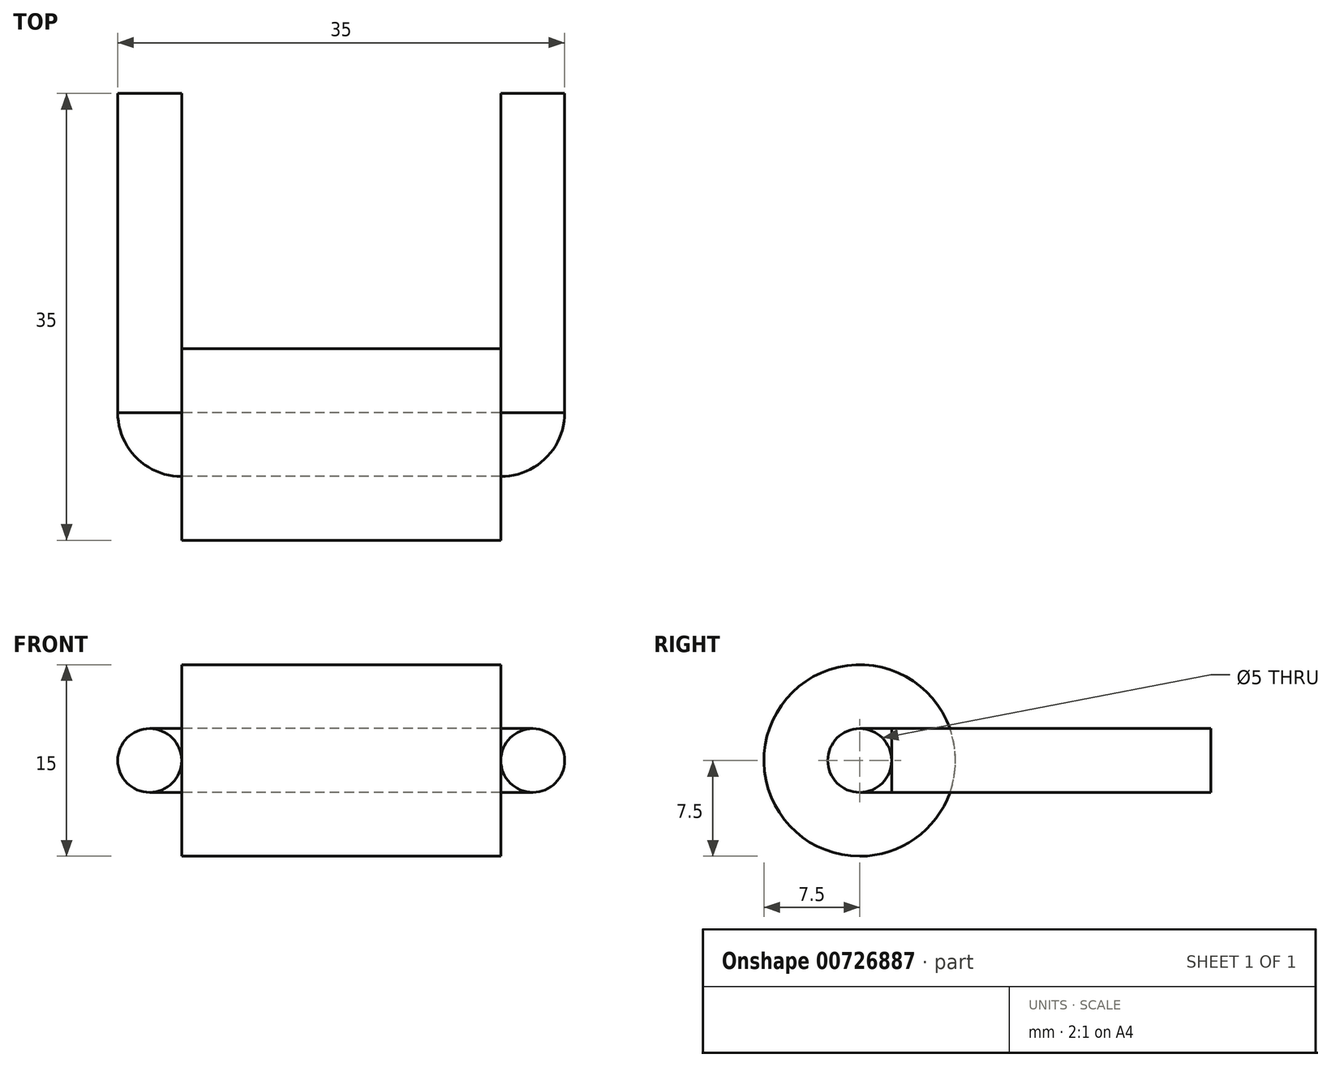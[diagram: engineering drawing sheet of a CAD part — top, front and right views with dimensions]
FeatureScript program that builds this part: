
annotation { "Feature Type Name" : "Feature", "Feature Type Description" : "" }
export const myFeature = defineFeature(function(context is Context, id is Id, definition is map)
    precondition{}
    {
        {
            var Q0;
            Q0=qCreatedBy(makeId("Front.planeOp"),FACE);
            var sketch = newSketch(context, id + "F0", { "sketchPlane" : qUnion([Q0])});
            skCircle(sketch, "E0", {"center": v(0, 0) * mm, "radius": 2.5 * mm});
            skLineSegment(sketch, "E1", {"start": v(0.18, 0) * mm, "end": v(2.5, 0) * mm});
            skCircle(sketch, "E2", {"center": v(30, 0) * mm, "radius": 2.5 * mm});
            skLineSegment(sketch, "E3.trimOffspring", {"start": v(27.5, 0) * mm, "end": v(30, 0) * mm});
            skSolve(sketch);
        }
        {
            var Q0;
            Q0 = qSketchRegion(id + "F0", true);
            extrude(context, id + "F1", {"entities" : qUnion([Q0]), "depth" : 25 * mm, "offsetDistance" : 25 * mm});
        }
        {
            var Q0;
            Q0=qCreatedBy(makeId("Front.planeOp"),FACE);
            cPlane(context, id + "F2", {"entities" : qUnion([Q0]), "cplaneType" : CPlaneType.OFFSET, "offset" : 27.5 * mm, "width" : 150 * mm, "height" : 150 * mm});
        }
        {
            var Q0;
            Q0=qCreatedBy(id+"F2.planeOp",FACE);
            var sketch = newSketch(context, id + "F3", { "sketchPlane" : qUnion([Q0])});
            skLineSegment(sketch, "E4", {"start": v(2.5, 0) * mm, "end": v(2.5, 2.5) * mm});
            skLineSegment(sketch, "E5", {"start": v(2.5, 2.5) * mm, "end": v(27.5, 2.5) * mm});
            skLineSegment(sketch, "E6", {"start": v(27.5, 2.5) * mm, "end": v(27.5, 0) * mm});
            skLineSegment(sketch, "E7", {"start": v(27.5, 0) * mm, "end": v(2.5, 0) * mm});
            skSolve(sketch);
        }
        {
            var Q0;
            Q0=makeQuery(id+"F3.imprint","IMPRINT",FACE,{"disambiguationData":[TD([[makeQuery(id+"F3.imprint","IMPRINT",EDGE,{"derivedFrom":sQuery(id+"F3.wireOp",EDGE,"E4")}),-1.0]])]});
            var Q1;
            Q1=sQuery(id+"F3.wireOp",EDGE,"E7");
            revolve(context, id + "F4", {"surfaceOperationType" : NewSurfaceOperationType.NEW, "entities" : qUnion([Q0]), "axis" : qUnion([Q1]), "revolveType" : RevolveType.FULL});
        }
        {
            var Q0;
            Q0=qCreatedBy(makeId("Top.planeOp"),FACE);
            var sketch = newSketch(context, id + "F5", { "sketchPlane" : qUnion([Q0])});
            skArc(sketch, "E8", {"start": v(0, -25) * mm, "mid": v(0.73, -26.77) * mm, "end": v(2.5, -27.5) * mm});
            skArc(sketch, "E9", {"start": v(27.5, -27.5) * mm, "mid": v(29.27, -26.77) * mm, "end": v(30, -25) * mm});
            skSolve(sketch);
        }
        {
            var Q0;
            Q0=makeQuery(id+"F1.opExtrude","CAP_FACE",FACE,{"disambiguationData":[OSD([sQuery(id+"F0.wireOp",EDGE,"E0")])],"isStart":false});
            var Q1;
            Q1=sQuery(id+"F5.wireOp",EDGE,"E8");
            sweep(context, id + "F6", {"profiles" : qUnion([Q0]), "path" : qUnion([Q1])});
        }
        {
            var Q0;
            Q0=qCreatedBy(makeId("Top.planeOp"),FACE);
            var sketch = newSketch(context, id + "F7", { "sketchPlane" : qUnion([Q0])});
            skArc(sketch, "E10", {"start": v(27.5, -27.5) * mm, "mid": v(29.27, -26.77) * mm, "end": v(30, -25) * mm});
            skSolve(sketch);
        }
        {
            var Q0;
            Q0=qCreatedBy(makeId("Right.planeOp"),FACE);
            cPlane(context, id + "F8", {"entities" : qUnion([Q0]), "cplaneType" : CPlaneType.OFFSET, "offset" : 2.5 * mm, "width" : 150 * mm, "height" : 150 * mm});
        }
        {
            var Q0;
            Q0=qCreatedBy(id+"F8.planeOp",FACE);
            var sketch = newSketch(context, id + "F9", { "sketchPlane" : qUnion([Q0])});
            skCircle(sketch, "E11", {"center": v(-27.5, 0) * mm, "radius": 2.5 * mm});
            skCircle(sketch, "E12", {"center": v(-27.5, 0) * mm, "radius": 7.5 * mm});
            skSolve(sketch);
        }
        {
            var Q0;
            Q0=makeQuery(id+"F9.imprint","IMPRINT",FACE,{"disambiguationData":[TD([[makeQuery(id+"F9.imprint","IMPRINT",EDGE,{"derivedFrom":sQuery(id+"F9.wireOp",EDGE,"E11")}),-1.0]])]});
            extrude(context, id + "F10", {"entities" : qUnion([Q0]), "depth" : 25 * mm, "offsetDistance" : 25 * mm});
        }
        {
            var Q0;
            Q0=makeQuery(id+"F1.opExtrude","CAP_FACE",FACE,{"disambiguationData":[OSD([sQuery(id+"F0.wireOp",EDGE,"E2")])],"isStart":false});
            var Q1;
            Q1 = qConstructionFilter(qBodyType(qCreatedBy(id + "F7" ,EDGE), BodyType.WIRE), ConstructionObject.NO);
            sweep(context, id + "F11", {"profiles" : qUnion([Q0]), "path" : qUnion([Q1])});
        }
    });
